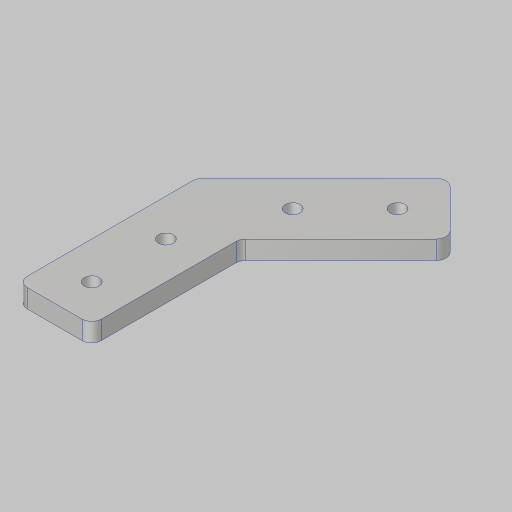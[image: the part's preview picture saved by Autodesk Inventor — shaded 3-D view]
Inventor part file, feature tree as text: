
AUTODESK INVENTOR PART (.ipt)
format: ipt  version: 2023.5 (Build 275446000, 446)  size: 197,120 bytes
history: native  units: in
note: dims shown in document units (in); Inventor stores cm internally (conversion verified against a paired STEP export)
features: sketch x2, extrude x1, hole x1, fillet x1, projected_geometry x1
ambient origin geometry x8: Origin, YZ Plane, XZ Plane, XY Plane, X Axis, Y Axis, Z Axis, Center Point
bodies: Solid1 (feature_tree)
feature tree (6):
  extrude  "Extrusion1"  Depth=1.0in
  hole  "Hole1"  [1 undecoded]
  fillet  "Fillet1"  Radius=2.0in
  sketch  "Sketch1"  dims[d0=1.0in d2=1.0in]
  sketch  "Sketch2"  dims[d4=135.0deg d8=2.0in d9=2.0in d10=0.25in d11=0.0in d12=1.0in d13=0.5in d14=1.0in d15=0.5in d16=0.201in d17=0.38in d18=0.385in d19=0.25in d20=0.5635in d21=1.0in d22=0.8108in d23=0.13in]
  projected_geometry  "Project Cut Edges1"
note: 1 required parameter value undecoded (feature->parameter linkage not recoverable at this tier; creation-order binding heuristic only, values carry confidence <= 0.55)
